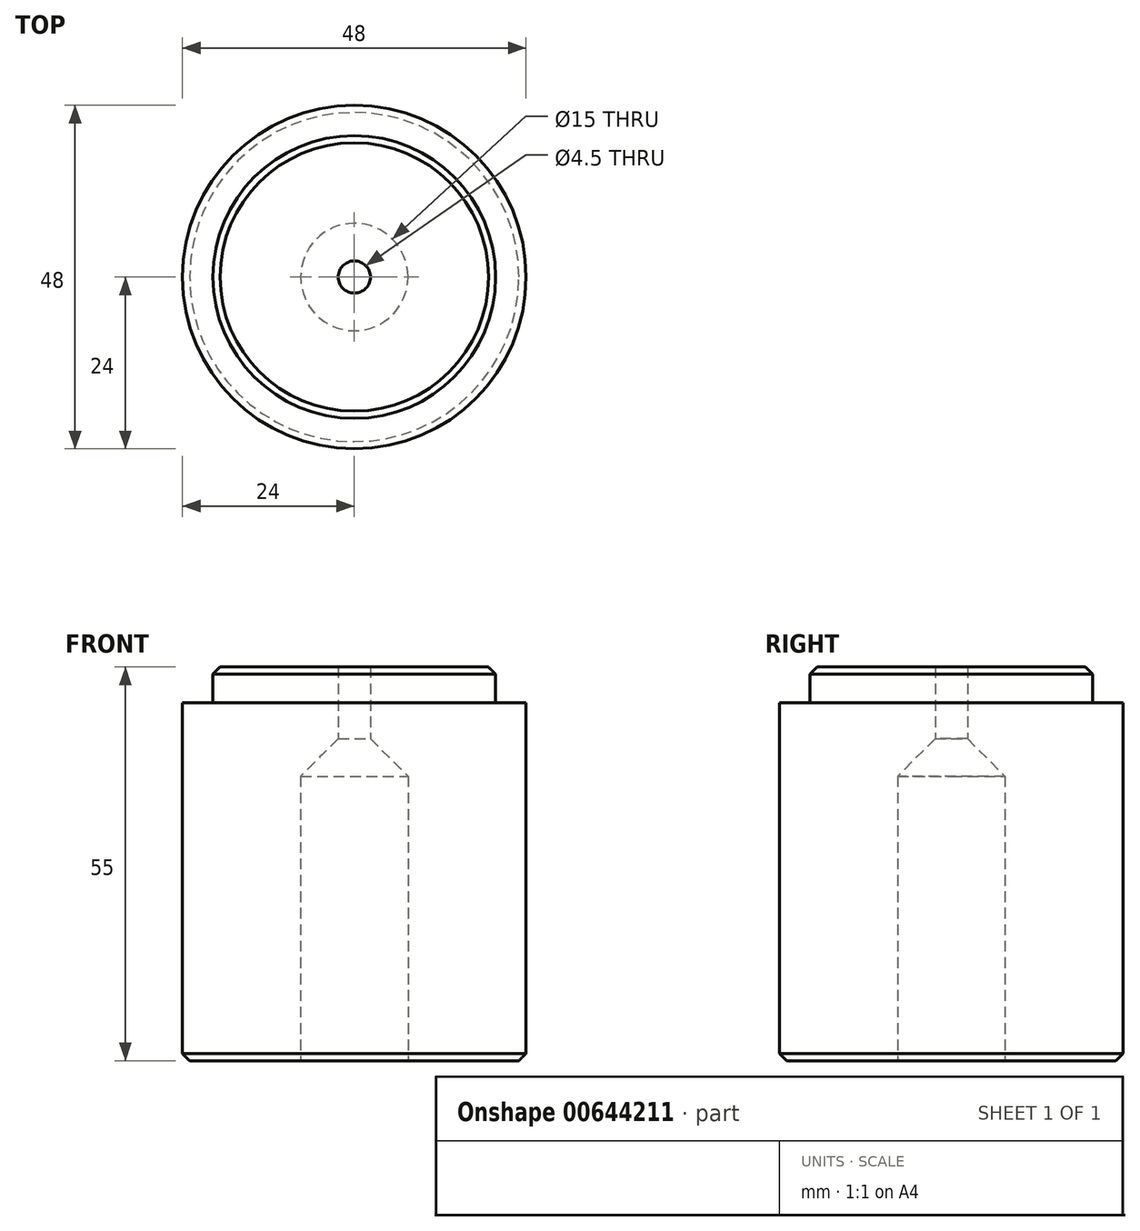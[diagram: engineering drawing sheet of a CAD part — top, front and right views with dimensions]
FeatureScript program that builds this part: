
annotation { "Feature Type Name" : "Feature", "Feature Type Description" : "" }
export const myFeature = defineFeature(function(context is Context, id is Id, definition is map)
    precondition{}
    {
        {
            var Q0;
            Q0=qCreatedBy(makeId("Top.planeOp"),FACE);
            var sketch = newSketch(context, id + "F0", { "sketchPlane" : qUnion([Q0])});
            skCircle(sketch, "E0", {"center": v(0, 0) * mm, "radius": 24 * mm});
            skSolve(sketch);
        }
        {
            var Q0;
            Q0=makeQuery(id+"F0.imprint","IMPRINT",FACE,{"disambiguationData":[TD([[makeQuery(id+"F0.imprint","IMPRINT",EDGE,{"derivedFrom":sQuery(id+"F0.wireOp",EDGE,"E0")}),1.0]])]});
            extrude(context, id + "F1", {"entities" : qUnion([Q0]), "depth" : 50 * mm, "offsetDistance" : 25 * mm});
        }
        {
            var Q0;
            Q0=makeQuery(id+"F1.opExtrude","CAP_FACE",FACE,{"disambiguationData":[OSD([sQuery(id+"F0.wireOp",EDGE,"E0")])],"isStart":false});
            var sketch = newSketch(context, id + "F2", { "sketchPlane" : qUnion([Q0])});
            skCircle(sketch, "E1", {"center": v(0, 0) * mm, "radius": 19.75 * mm});
            skSolve(sketch);
        }
        {
            var Q0;
            Q0=makeQuery(id+"F2.imprint","IMPRINT",FACE,{"disambiguationData":[TD([[makeQuery(id+"F2.imprint","IMPRINT",EDGE,{"derivedFrom":sQuery(id+"F2.wireOp",EDGE,"E1")}),1.0]])]});
            extrude(context, id + "F3", {"entities" : qUnion([Q0]), "operationType" : NewBodyOperationType.ADD, "depth" : 5 * mm, "offsetDistance" : 25 * mm});
        }
        {
            var Q0;
            Q0=makeQuery(id+"F1.opExtrude","CAP_FACE",FACE,{"disambiguationData":[OSD([sQuery(id+"F0.wireOp",EDGE,"E0")])],"isStart":true});
            var sketch = newSketch(context, id + "F4", { "sketchPlane" : qUnion([Q0])});
            skCircle(sketch, "E2", {"center": v(0, 0) * mm, "radius": 7.5 * mm});
            skSolve(sketch);
        }
        {
            var Q0;
            Q0=makeQuery(id+"F4.imprint","IMPRINT",FACE,{"disambiguationData":[TD([[makeQuery(id+"F4.imprint","IMPRINT",EDGE,{"derivedFrom":sQuery(id+"F4.wireOp",EDGE,"E2")}),1.0]])]});
            extrude(context, id + "F5", {"entities" : qUnion([Q0]), "operationType" : NewBodyOperationType.REMOVE, "oppositeDirection" : true, "depth" : 45 * mm, "offsetDistance" : 25 * mm});
        }
        {
            var Q0;
            Q0=makeQuery(id+"F5.boolean.opBoolean","COPY",FACE,{"derivedFrom":makeQuery(id+"F5.opExtrude","CAP_FACE",FACE,{"disambiguationData":[OSD([sQuery(id+"F4.wireOp",EDGE,"E2")])],"isStart":false})});
            var sketch = newSketch(context, id + "F6", { "sketchPlane" : qUnion([Q0])});
            skCircle(sketch, "E3", {"center": v(0, 0) * mm, "radius": 2.25 * mm});
            skSolve(sketch);
        }
        {
            var Q0;
            Q0=makeQuery(id+"F6.imprint","IMPRINT",FACE,{"disambiguationData":[TD([[makeQuery(id+"F6.imprint","IMPRINT",EDGE,{"derivedFrom":sQuery(id+"F6.wireOp",EDGE,"E3")}),1.0]])]});
            extrude(context, id + "F7", {"entities" : qUnion([Q0]), "operationType" : NewBodyOperationType.REMOVE, "oppositeDirection" : true, "depth" : 10 * mm, "offsetDistance" : 25 * mm});
        }
        {
            var Q0;
            Q0=makeQuery(id+"F1.opExtrude","CAP_EDGE",EDGE,{"disambiguationData":[OSD([sQuery(id+"F0.wireOp",EDGE,"E0")])],"isStart":true});
            var Q1;
            Q1=makeQuery(id+"F5.boolean.opBoolean","COPY",EDGE,{"derivedFrom":makeQuery(id+"F5.opExtrude","CAP_EDGE",EDGE,{"disambiguationData":[OSD([sQuery(id+"F4.wireOp",EDGE,"E2")])],"isStart":true})});
            var Q2;
            Q2=makeQuery(id+"F3.opExtrude","CAP_EDGE",EDGE,{"disambiguationData":[OSD([sQuery(id+"F2.wireOp",EDGE,"E1")])],"isStart":false});
            chamfer(context, id + "F8", {"entities" : qUnion([Q0, Q1, Q2]), "width" : 1 * mm, "tangentPropagation" : true});
        }
        {
            var Q0;
            Q0=makeQuery(id+"F5.boolean.opBoolean","COPY",EDGE,{"derivedFrom":makeQuery(id+"F5.opExtrude","CAP_EDGE",EDGE,{"disambiguationData":[OSD([sQuery(id+"F4.wireOp",EDGE,"E2")])],"isStart":false})});
            chamfer(context, id + "F9", {"entities" : qUnion([Q0]), "width" : 5.25 * mm, "tangentPropagation" : true});
        }
    });
